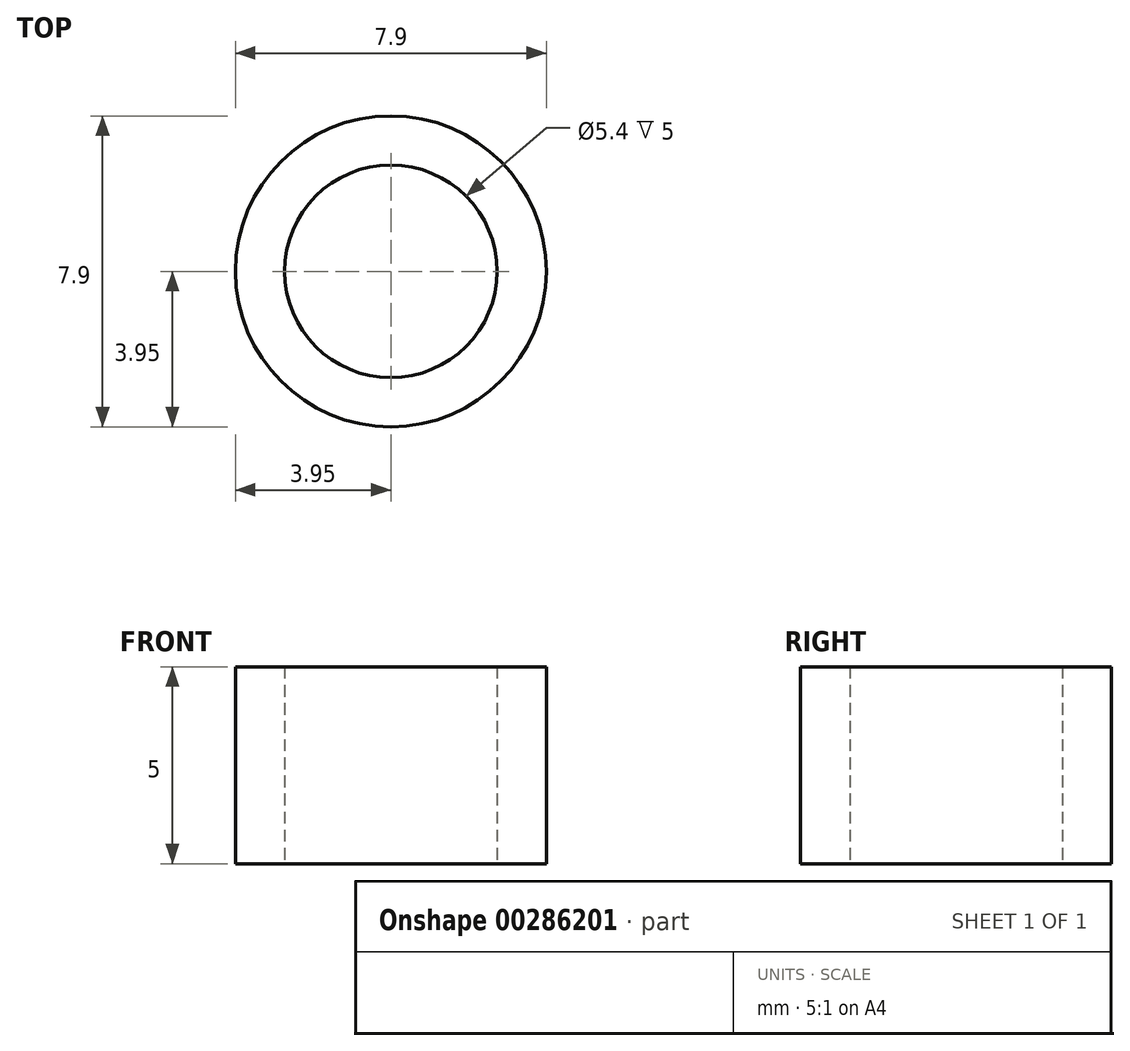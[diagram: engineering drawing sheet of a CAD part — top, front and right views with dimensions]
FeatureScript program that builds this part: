
annotation { "Feature Type Name" : "Feature", "Feature Type Description" : "" }
export const myFeature = defineFeature(function(context is Context, id is Id, definition is map)
    precondition{}
    {
        {
            var Q0;
            Q0=qCreatedBy(makeId("Top.planeOp"),FACE);
            var sketch = newSketch(context, id + "F0", { "sketchPlane" : qUnion([Q0])});
            skCircle(sketch, "E0", {"center": v(0, 0) * mm, "radius": 2.7 * mm});
            skCircle(sketch, "E1", {"center": v(0, 0) * mm, "radius": 3.95 * mm});
            skSolve(sketch);
        }
        {
            var Q0;
            Q0=makeQuery(id+"F0.imprint","IMPRINT",FACE,{"disambiguationData":[TD([[makeQuery(id+"F0.imprint","IMPRINT",EDGE,{"derivedFrom":sQuery(id+"F0.wireOp",EDGE,"E0")}),-1.0]])]});
            extrude(context, id + "F1", {"entities" : qUnion([Q0]), "depth" : 5 * mm});
        }
    });
